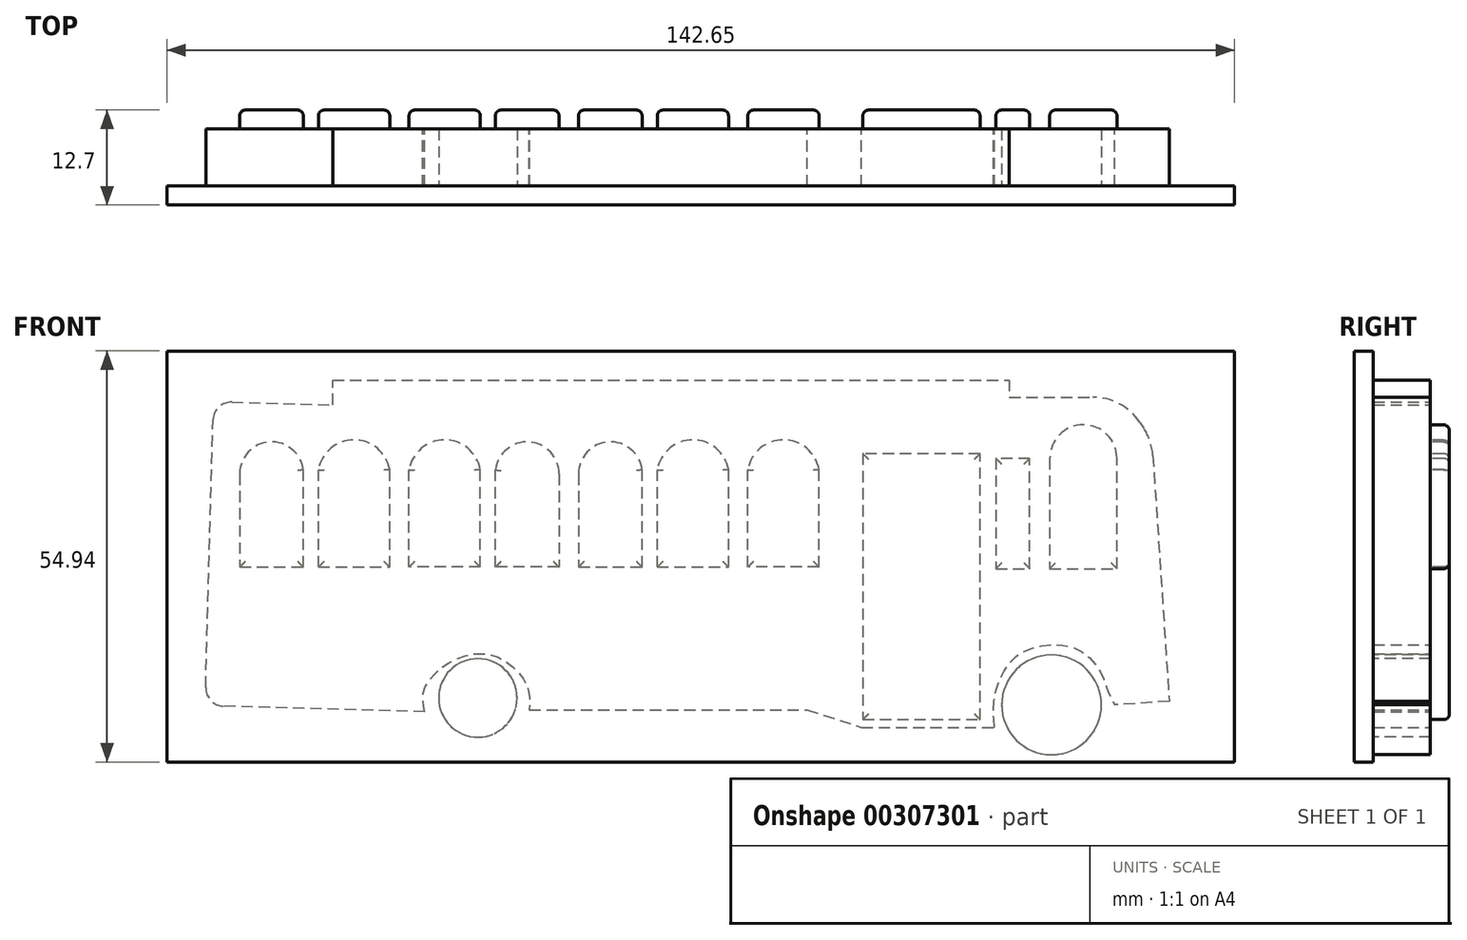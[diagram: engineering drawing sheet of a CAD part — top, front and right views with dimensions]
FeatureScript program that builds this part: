
annotation { "Feature Type Name" : "Feature", "Feature Type Description" : "" }
export const myFeature = defineFeature(function(context is Context, id is Id, definition is map)
    precondition{}
    {
        {
            var Q0;
            Q0=qCreatedBy(makeId("Front.planeOp"),FACE);
            var sketch = newSketch(context, id + "F0", { "sketchPlane" : qUnion([Q0])});
            skLineSegment(sketch, "E0", {"start": v(39.8, -36.02) * mm, "end": v(3.64, -36.02) * mm});
            skLineSegment(sketch, "E1", {"start": v(-11.3, -36.26) * mm, "end": v(-40.63, -35.46) * mm});
            skLineSegment(sketch, "E2", {"start": v(-40.63, -35.46) * mm, "end": v(-39.52, 5.2) * mm});
            skLineSegment(sketch, "E3", {"start": v(-39.52, 5.2) * mm, "end": v(-23.59, 4.75) * mm});
            skLineSegment(sketch, "E4", {"start": v(-23.59, 4.75) * mm, "end": v(-23.59, 8.08) * mm});
            skLineSegment(sketch, "E5", {"start": v(-23.59, 8.08) * mm, "end": v(66.8, 8.08) * mm});
            skLineSegment(sketch, "E6", {"start": v(66.8, 8.08) * mm, "end": v(66.8, 5.8) * mm});
            skLineSegment(sketch, "E7", {"start": v(66.8, 5.8) * mm, "end": v(81.99, 5.8) * mm});
            skLineSegment(sketch, "E8", {"start": v(81.99, 5.8) * mm, "end": v(85.84, 0) * mm});
            skLineSegment(sketch, "E9", {"start": v(85.84, 0) * mm, "end": v(88.18, -34.85) * mm});
            skLineSegment(sketch, "E10", {"start": v(88.18, -34.85) * mm, "end": v(80.86, -35.34) * mm});
            skLineSegment(sketch, "E11", {"start": v(39.8, -36.02) * mm, "end": v(47.06, -38.36) * mm});
            skLineSegment(sketch, "E12", {"start": v(47.06, -38.36) * mm, "end": v(64.81, -38.36) * mm});
            skFitSpline(sketch, "E13", {"points": [v(-11.3, -36.26) * mm, v(-11.3, -33.09) * mm, v(-6.88, -29.1) * mm, v(-1.23, -29.1) * mm, v(2.39, -32.9) * mm, v(2.67, -36.02) * mm], "startDerivative": vector(-3.97, 18.55) * mm, "endDerivative": vector(-1.35, -18.22) * mm});
            skLineSegment(sketch, "E14", {"start": v(2.67, -36.02) * mm, "end": v(3.64, -36.02) * mm});
            skFitSpline(sketch, "E15", {"points": [v(64.81, -38.36) * mm, v(64.81, -34.47) * mm, v(66.9, -29.62) * mm, v(70.47, -27.57) * mm, v(75.5, -27.75) * mm, v(78.77, -30.61) * mm, v(79.88, -33.24) * mm, v(80.86, -35.34) * mm], "startDerivative": vector(-2.47, 25.93) * mm, "endDerivative": vector(9.48, -18.57) * mm});
            skSolve(sketch);
        }
        {
            var Q0;
            Q0=makeQuery(id+"F0.imprint","IMPRINT",FACE,{"disambiguationData":[TD([[makeQuery(id+"F0.imprint","IMPRINT",EDGE,{"derivedFrom":sQuery(id+"F0.wireOp",EDGE,"E0")}),-1.0]])]});
            extrude(context, id + "F1", {"entities" : qUnion([Q0]), "depth" : 7.62 * mm});
        }
        {
            var Q0;
            Q0=makeQuery(id+"F1.opExtrude","SWEPT_EDGE",EDGE,{"disambiguationData":[OSD([sQuery(id+"F0.wireOp",EDGE,"E2"),sQuery(id+"F0.wireOp",EDGE,"E3")])]});
            var Q1;
            Q1=makeQuery(id+"F1.opExtrude","SWEPT_EDGE",EDGE,{"disambiguationData":[OSD([sQuery(id+"F0.wireOp",EDGE,"E1"),sQuery(id+"F0.wireOp",EDGE,"E2")])]});
            fillet(context, id + "F2", {"entities" : qUnion([Q0, Q1]), "radius" : 2.45 * mm, "tangentPropagation" : true, "allowEdgeOverflow" : false});
        }
        {
            var Q0;
            Q0=makeQuery(id+"F1.opExtrude","SWEPT_EDGE",EDGE,{"disambiguationData":[OSD([sQuery(id+"F0.wireOp",EDGE,"E8"),sQuery(id+"F0.wireOp",EDGE,"E9")])]});
            var Q1;
            Q1=makeQuery(id+"F1.opExtrude","SWEPT_EDGE",EDGE,{"disambiguationData":[OSD([sQuery(id+"F0.wireOp",EDGE,"E7"),sQuery(id+"F0.wireOp",EDGE,"E8")])]});
            fillet(context, id + "F3", {"entities" : qUnion([Q0, Q1]), "radius" : 7.55 * mm, "tangentPropagation" : true, "allowEdgeOverflow" : false});
        }
        {
            var Q0;
            Q0=makeQuery(id+"F1.opExtrude","CAP_FACE",FACE,{"disambiguationData":[OSD([sQuery(id+"F0.wireOp",EDGE,"E0"),sQuery(id+"F0.wireOp",EDGE,"E1"),sQuery(id+"F0.wireOp",EDGE,"E2"),sQuery(id+"F0.wireOp",EDGE,"E3"),sQuery(id+"F0.wireOp",EDGE,"E4"),sQuery(id+"F0.wireOp",EDGE,"E5"),sQuery(id+"F0.wireOp",EDGE,"E6"),sQuery(id+"F0.wireOp",EDGE,"E7"),sQuery(id+"F0.wireOp",EDGE,"E8"),sQuery(id+"F0.wireOp",EDGE,"E9"),sQuery(id+"F0.wireOp",EDGE,"E10"),sQuery(id+"F0.wireOp",EDGE,"E11"),sQuery(id+"F0.wireOp",EDGE,"E12"),sQuery(id+"F0.wireOp",EDGE,"E13"),sQuery(id+"F0.wireOp",EDGE,"E14"),sQuery(id+"F0.wireOp",EDGE,"E15")])],"isStart":false});
            var sketch = newSketch(context, id + "F4", { "sketchPlane" : qUnion([Q0])});
            skLineSegment(sketch, "E16", {"start": v(-36.02, -4.45) * mm, "end": v(-36.02, -16.93) * mm});
            skLineSegment(sketch, "E17", {"start": v(-36.02, -16.93) * mm, "end": v(-27.53, -16.93) * mm});
            skLineSegment(sketch, "E18", {"start": v(-27.53, -16.93) * mm, "end": v(-27.53, -3.96) * mm});
            skArc(sketch, "E19", {"start": v(-27.53, -3.96) * mm, "mid": v(-32, -0.2) * mm, "end": v(-36.02, -4.45) * mm});
            skLineSegment(sketch, "E20", {"start": v(47.23, -1.77) * mm, "end": v(47.23, -37.3) * mm});
            skLineSegment(sketch, "E21", {"start": v(47.23, -37.3) * mm, "end": v(62.9, -37.3) * mm});
            skLineSegment(sketch, "E22", {"start": v(62.9, -37.3) * mm, "end": v(62.9, -1.77) * mm});
            skLineSegment(sketch, "E23", {"start": v(62.9, -1.77) * mm, "end": v(47.23, -1.77) * mm});
            skLineSegment(sketch, "E24", {"start": v(47.23, -10.92) * mm, "end": v(55.06, -10.92) * mm, "construction": true});
            skLineSegment(sketch, "E25", {"start": v(55.06, -1.77) * mm, "end": v(55.06, -37.3) * mm});
            skLineSegment(sketch, "E26", {"start": v(-25.5, -16.93) * mm, "end": v(-15.98, -16.93) * mm});
            skLineSegment(sketch, "E27", {"start": v(-15.98, -16.93) * mm, "end": v(-15.98, -3.91) * mm});
            skLineSegment(sketch, "E28", {"start": v(-25.5, -16.93) * mm, "end": v(-25.5, -3.91) * mm});
            skArc(sketch, "E29", {"start": v(-15.98, -3.91) * mm, "mid": v(-20.74, 0.08) * mm, "end": v(-25.5, -3.91) * mm});
            skLineSegment(sketch, "E30", {"start": v(-14.7, 2.62) * mm, "end": v(-14.7, -16.9) * mm, "construction": true});
            skArc(sketch, "E31.MirrorCS", {"start": v(-13.4, -3.91) * mm, "mid": v(-8.64, 0.08) * mm, "end": v(-3.88, -3.91) * mm});
            skArc(sketch, "E32.MirrorCS", {"start": v(-1.86, -3.96) * mm, "mid": v(2.62, -0.2) * mm, "end": v(6.64, -4.45) * mm});
            skLineSegment(sketch, "E33.MirrorCS", {"start": v(6.64, -4.45) * mm, "end": v(6.64, -16.93) * mm});
            skLineSegment(sketch, "E34.MirrorCS", {"start": v(-1.86, -16.93) * mm, "end": v(-1.86, -3.96) * mm});
            skLineSegment(sketch, "E35.MirrorCS", {"start": v(-3.88, -16.93) * mm, "end": v(-3.88, -3.91) * mm});
            skLineSegment(sketch, "E36.MirrorCS", {"start": v(-13.4, -16.93) * mm, "end": v(-13.4, -3.91) * mm});
            skLineSegment(sketch, "E37.MirrorCS", {"start": v(-3.88, -16.93) * mm, "end": v(-13.4, -16.93) * mm});
            skLineSegment(sketch, "E38.MirrorCS", {"start": v(6.64, -16.93) * mm, "end": v(-1.86, -16.93) * mm});
            skLineSegment(sketch, "E39", {"start": v(-15.98, -9.71) * mm, "end": v(-14.7, -9.71) * mm, "construction": true});
            skLineSegment(sketch, "E40", {"start": v(6.64, -10.22) * mm, "end": v(7.94, -10.22) * mm, "construction": true});
            skLineSegment(sketch, "E41", {"start": v(7.94, -10.22) * mm, "end": v(7.94, 0) * mm, "construction": true});
            skLineSegment(sketch, "E42", {"start": v(7.94, 0) * mm, "end": v(7.94, -17.88) * mm, "construction": true});
            skArc(sketch, "E43.MirrorCS", {"start": v(17.74, -3.96) * mm, "mid": v(13.26, -0.2) * mm, "end": v(9.24, -4.45) * mm});
            skArc(sketch, "E44.MirrorCS", {"start": v(29.28, -3.91) * mm, "mid": v(24.52, 0.08) * mm, "end": v(19.76, -3.91) * mm});
            skArc(sketch, "E45.MirrorCS", {"start": v(31.87, -3.91) * mm, "mid": v(36.62, 0.08) * mm, "end": v(41.38, -3.91) * mm});
            skLineSegment(sketch, "E46.MirrorCS", {"start": v(17.74, -16.93) * mm, "end": v(17.74, -3.96) * mm});
            skLineSegment(sketch, "E47.MirrorCS", {"start": v(9.24, -4.45) * mm, "end": v(9.24, -16.93) * mm});
            skLineSegment(sketch, "E48.MirrorCS", {"start": v(19.76, -16.93) * mm, "end": v(19.76, -3.91) * mm});
            skLineSegment(sketch, "E49.MirrorCS", {"start": v(29.28, -16.93) * mm, "end": v(29.28, -3.91) * mm});
            skLineSegment(sketch, "E50.MirrorCS", {"start": v(31.87, -16.93) * mm, "end": v(31.87, -3.91) * mm});
            skLineSegment(sketch, "E51.MirrorCS", {"start": v(41.38, -16.93) * mm, "end": v(41.38, -3.91) * mm});
            skLineSegment(sketch, "E52.MirrorCS", {"start": v(41.38, -16.93) * mm, "end": v(31.87, -16.93) * mm});
            skLineSegment(sketch, "E53.MirrorCS", {"start": v(19.76, -16.93) * mm, "end": v(29.28, -16.93) * mm});
            skLineSegment(sketch, "E54.MirrorCS", {"start": v(9.24, -16.93) * mm, "end": v(17.74, -16.93) * mm});
            skLineSegment(sketch, "E55", {"start": v(65.01, -17.13) * mm, "end": v(69.53, -17.13) * mm});
            skLineSegment(sketch, "E56", {"start": v(69.53, -17.13) * mm, "end": v(69.53, -2.4) * mm});
            skLineSegment(sketch, "E57", {"start": v(69.53, -2.4) * mm, "end": v(65.01, -2.4) * mm});
            skLineSegment(sketch, "E58", {"start": v(65.01, -2.4) * mm, "end": v(65.01, -17.13) * mm});
            skLineSegment(sketch, "E59", {"start": v(71.76, -17.13) * mm, "end": v(81.84, -17.13) * mm});
            skPoint(sketch, "E59.startSnap0", {"position": v(67.27, -17.13) * mm});
            skLineSegment(sketch, "E60", {"start": v(81.84, -17.13) * mm, "end": v(81.84, -2.34) * mm});
            skLineSegment(sketch, "E61", {"start": v(71.76, -17.13) * mm, "end": v(71.76, -2.34) * mm});
            skArc(sketch, "E62", {"start": v(81.84, -2.4) * mm, "mid": v(76.88, 2.07) * mm, "end": v(71.82, -2.28) * mm});
            skSolve(sketch);
        }
        {
            var Q0;
            Q0 = qSketchRegion(id + "F4", true);
            extrude(context, id + "F5", {"entities" : qUnion([Q0]), "operationType" : NewBodyOperationType.ADD, "oppositeDirection" : true, "depth" : 10.16 * mm});
        }
        {
            var Q0;
            Q0=makeQuery(id+"F1.opExtrude","CAP_FACE",FACE,{"disambiguationData":[OSD([sQuery(id+"F0.wireOp",EDGE,"E0"),sQuery(id+"F0.wireOp",EDGE,"E1"),sQuery(id+"F0.wireOp",EDGE,"E2"),sQuery(id+"F0.wireOp",EDGE,"E3"),sQuery(id+"F0.wireOp",EDGE,"E4"),sQuery(id+"F0.wireOp",EDGE,"E5"),sQuery(id+"F0.wireOp",EDGE,"E6"),sQuery(id+"F0.wireOp",EDGE,"E7"),sQuery(id+"F0.wireOp",EDGE,"E8"),sQuery(id+"F0.wireOp",EDGE,"E9"),sQuery(id+"F0.wireOp",EDGE,"E10"),sQuery(id+"F0.wireOp",EDGE,"E11"),sQuery(id+"F0.wireOp",EDGE,"E12"),sQuery(id+"F0.wireOp",EDGE,"E13"),sQuery(id+"F0.wireOp",EDGE,"E14"),sQuery(id+"F0.wireOp",EDGE,"E15")])],"isStart":true});
            var sketch = newSketch(context, id + "F6", { "sketchPlane" : qUnion([Q0])});
            skLineSegment(sketch, "E63", {"start": v(-72.2, -17.13) * mm, "end": v(-81.18, -17.13) * mm});
            skLineSegment(sketch, "E64", {"start": v(-81.18, -17.13) * mm, "end": v(-81.18, -9.92) * mm});
            skLineSegment(sketch, "E65", {"start": v(-81.18, -9.92) * mm, "end": v(-81.18, -2.4) * mm});
            skLineSegment(sketch, "E66", {"start": v(-72.2, -2.4) * mm, "end": v(-72.2, -17.13) * mm});
            skArc(sketch, "E67", {"start": v(-72.2, -2.4) * mm, "mid": v(-76.7, 2.09) * mm, "end": v(-81.18, -2.4) * mm});
            skSolve(sketch);
        }
        {
            var Q0;
            Q0 = qSketchRegion(id + "F6", true);
            extrude(context, id + "F7", {"entities" : qUnion([Q0]), "operationType" : NewBodyOperationType.ADD, "depth" : 2.54 * mm});
        }
        {
            var Q0;
            Q0=makeQuery(id+"F1.opExtrude","CAP_FACE",FACE,{"disambiguationData":[OSD([sQuery(id+"F0.wireOp",EDGE,"E0"),sQuery(id+"F0.wireOp",EDGE,"E1"),sQuery(id+"F0.wireOp",EDGE,"E2"),sQuery(id+"F0.wireOp",EDGE,"E3"),sQuery(id+"F0.wireOp",EDGE,"E4"),sQuery(id+"F0.wireOp",EDGE,"E5"),sQuery(id+"F0.wireOp",EDGE,"E6"),sQuery(id+"F0.wireOp",EDGE,"E7"),sQuery(id+"F0.wireOp",EDGE,"E8"),sQuery(id+"F0.wireOp",EDGE,"E9"),sQuery(id+"F0.wireOp",EDGE,"E10"),sQuery(id+"F0.wireOp",EDGE,"E11"),sQuery(id+"F0.wireOp",EDGE,"E12"),sQuery(id+"F0.wireOp",EDGE,"E13"),sQuery(id+"F0.wireOp",EDGE,"E14"),sQuery(id+"F0.wireOp",EDGE,"E15")])],"isStart":false});
            var sketch = newSketch(context, id + "F8", { "sketchPlane" : qUnion([Q0])});
            skLineSegment(sketch, "E68.bottom", {"start": v(-45.74, 11.96) * mm, "end": v(96.9, 11.96) * mm});
            skLineSegment(sketch, "E68.top", {"start": v(-45.74, -42.98) * mm, "end": v(96.9, -42.98) * mm});
            skLineSegment(sketch, "E68.left", {"start": v(-45.74, 11.96) * mm, "end": v(-45.74, -42.98) * mm});
            skLineSegment(sketch, "E68.right", {"start": v(96.9, 11.96) * mm, "end": v(96.9, -42.98) * mm});
            skSolve(sketch);
        }
        {
            var Q0;
            Q0=makeQuery(id+"F8.imprint","IMPRINT",FACE,{"disambiguationData":[TD([[makeQuery(id+"F8.imprint","IMPRINT",EDGE,{"derivedFrom":sQuery(id+"F8.wireOp",EDGE,"E68.bottom")}),-1.0]])]});
            extrude(context, id + "F9", {"entities" : qUnion([Q0]), "depth" : 2.54 * mm});
        }
        {
            var Q0;
            Q0=makeQuery(id+"F1.opExtrude","CAP_FACE",FACE,{"disambiguationData":[OSD([sQuery(id+"F0.wireOp",EDGE,"E0"),sQuery(id+"F0.wireOp",EDGE,"E1"),sQuery(id+"F0.wireOp",EDGE,"E2"),sQuery(id+"F0.wireOp",EDGE,"E3"),sQuery(id+"F0.wireOp",EDGE,"E4"),sQuery(id+"F0.wireOp",EDGE,"E5"),sQuery(id+"F0.wireOp",EDGE,"E6"),sQuery(id+"F0.wireOp",EDGE,"E7"),sQuery(id+"F0.wireOp",EDGE,"E8"),sQuery(id+"F0.wireOp",EDGE,"E9"),sQuery(id+"F0.wireOp",EDGE,"E10"),sQuery(id+"F0.wireOp",EDGE,"E11"),sQuery(id+"F0.wireOp",EDGE,"E12"),sQuery(id+"F0.wireOp",EDGE,"E13"),sQuery(id+"F0.wireOp",EDGE,"E14"),sQuery(id+"F0.wireOp",EDGE,"E15")])],"isStart":false});
            extrude(context, id + "F10", {"entities" : qUnion([Q0]), "depth" : 2.54 * mm});
        }
        {
            var Q0;
            Q0=makeQuery(id+"F10.opExtrude","SWEPT_BODY",BODY,{"disambiguationData":[OSD([sQuery(id+"F0.wireOp",EDGE,"E0"),sQuery(id+"F0.wireOp",EDGE,"E1"),sQuery(id+"F0.wireOp",EDGE,"E2"),sQuery(id+"F0.wireOp",EDGE,"E3"),sQuery(id+"F0.wireOp",EDGE,"E4"),sQuery(id+"F0.wireOp",EDGE,"E5"),sQuery(id+"F0.wireOp",EDGE,"E6"),sQuery(id+"F0.wireOp",EDGE,"E7"),sQuery(id+"F0.wireOp",EDGE,"E8"),sQuery(id+"F0.wireOp",EDGE,"E9"),sQuery(id+"F0.wireOp",EDGE,"E10"),sQuery(id+"F0.wireOp",EDGE,"E11"),sQuery(id+"F0.wireOp",EDGE,"E12"),sQuery(id+"F0.wireOp",EDGE,"E13"),sQuery(id+"F0.wireOp",EDGE,"E14"),sQuery(id+"F0.wireOp",EDGE,"E15")])]});
            var Q1;
            Q1=makeQuery(id+"F9.opExtrude","SWEPT_BODY",BODY,{"disambiguationData":[OSD([sQuery(id+"F0.wireOp",EDGE,"E0"),sQuery(id+"F0.wireOp",EDGE,"E1"),sQuery(id+"F0.wireOp",EDGE,"E2"),sQuery(id+"F0.wireOp",EDGE,"E3"),sQuery(id+"F0.wireOp",EDGE,"E4"),sQuery(id+"F0.wireOp",EDGE,"E5"),sQuery(id+"F0.wireOp",EDGE,"E6"),sQuery(id+"F0.wireOp",EDGE,"E7"),sQuery(id+"F0.wireOp",EDGE,"E8"),sQuery(id+"F0.wireOp",EDGE,"E9"),sQuery(id+"F0.wireOp",EDGE,"E10"),sQuery(id+"F0.wireOp",EDGE,"E11"),sQuery(id+"F0.wireOp",EDGE,"E12"),sQuery(id+"F0.wireOp",EDGE,"E13"),sQuery(id+"F0.wireOp",EDGE,"E14"),sQuery(id+"F0.wireOp",EDGE,"E15"),sQuery(id+"F8.wireOp",EDGE,"E68.bottom"),sQuery(id+"F8.wireOp",EDGE,"E68.top"),sQuery(id+"F8.wireOp",EDGE,"E68.left"),sQuery(id+"F8.wireOp",EDGE,"E68.right")])]});
            var Q2;
            Q2=makeQuery(id+"F1.opExtrude","SWEPT_BODY",BODY,{"disambiguationData":[OSD([sQuery(id+"F0.wireOp",EDGE,"E0"),sQuery(id+"F0.wireOp",EDGE,"E1"),sQuery(id+"F0.wireOp",EDGE,"E2"),sQuery(id+"F0.wireOp",EDGE,"E3"),sQuery(id+"F0.wireOp",EDGE,"E4"),sQuery(id+"F0.wireOp",EDGE,"E5"),sQuery(id+"F0.wireOp",EDGE,"E6"),sQuery(id+"F0.wireOp",EDGE,"E7"),sQuery(id+"F0.wireOp",EDGE,"E8"),sQuery(id+"F0.wireOp",EDGE,"E9"),sQuery(id+"F0.wireOp",EDGE,"E10"),sQuery(id+"F0.wireOp",EDGE,"E11"),sQuery(id+"F0.wireOp",EDGE,"E12"),sQuery(id+"F0.wireOp",EDGE,"E13"),sQuery(id+"F0.wireOp",EDGE,"E14"),sQuery(id+"F0.wireOp",EDGE,"E15")])]});
            booleanBodies(context, id + "F11", {"operationType" : BooleanOperationType.UNION, "tools" : qUnion([Q0, Q1, Q2])});
        }
        {
            var Q0;
            Q0=makeQuery(id+"F7.opExtrude","CAP_FACE",FACE,{"disambiguationData":[OSD([sQuery(id+"F6.wireOp",EDGE,"E63"),sQuery(id+"F6.wireOp",EDGE,"E64"),sQuery(id+"F6.wireOp",EDGE,"E65"),sQuery(id+"F6.wireOp",EDGE,"E66"),sQuery(id+"F6.wireOp",EDGE,"E67")])],"isStart":false});
            var Q1;
            Q1=makeQuery(id+"F5.opExtrude","CAP_FACE",FACE,{"disambiguationData":[OSD([sQuery(id+"F4.wireOp",EDGE,"E55"),sQuery(id+"F4.wireOp",EDGE,"E56"),sQuery(id+"F4.wireOp",EDGE,"E57"),sQuery(id+"F4.wireOp",EDGE,"E58")])],"isStart":false});
            var Q2;
            Q2=makeQuery(id+"F5.opExtrude","CAP_FACE",FACE,{"disambiguationData":[OSD([sQuery(id+"F4.wireOp",EDGE,"E20"),sQuery(id+"F4.wireOp",EDGE,"E21"),sQuery(id+"F4.wireOp",EDGE,"E22"),sQuery(id+"F4.wireOp",EDGE,"E23")])],"isStart":false});
            var Q3;
            Q3=makeQuery(id+"F5.opExtrude","CAP_FACE",FACE,{"disambiguationData":[OSD([sQuery(id+"F4.wireOp",EDGE,"E45.MirrorCS"),sQuery(id+"F4.wireOp",EDGE,"E50.MirrorCS"),sQuery(id+"F4.wireOp",EDGE,"E51.MirrorCS"),sQuery(id+"F4.wireOp",EDGE,"E52.MirrorCS")])],"isStart":false});
            var Q4;
            Q4=makeQuery(id+"F5.opExtrude","CAP_FACE",FACE,{"disambiguationData":[OSD([sQuery(id+"F4.wireOp",EDGE,"E44.MirrorCS"),sQuery(id+"F4.wireOp",EDGE,"E48.MirrorCS"),sQuery(id+"F4.wireOp",EDGE,"E49.MirrorCS"),sQuery(id+"F4.wireOp",EDGE,"E53.MirrorCS")])],"isStart":false});
            var Q5;
            Q5=makeQuery(id+"F5.opExtrude","CAP_FACE",FACE,{"disambiguationData":[OSD([sQuery(id+"F4.wireOp",EDGE,"E43.MirrorCS"),sQuery(id+"F4.wireOp",EDGE,"E46.MirrorCS"),sQuery(id+"F4.wireOp",EDGE,"E47.MirrorCS"),sQuery(id+"F4.wireOp",EDGE,"E54.MirrorCS")])],"isStart":false});
            var Q6;
            Q6=makeQuery(id+"F5.opExtrude","CAP_FACE",FACE,{"disambiguationData":[OSD([sQuery(id+"F4.wireOp",EDGE,"E32.MirrorCS"),sQuery(id+"F4.wireOp",EDGE,"E33.MirrorCS"),sQuery(id+"F4.wireOp",EDGE,"E34.MirrorCS"),sQuery(id+"F4.wireOp",EDGE,"E38.MirrorCS")])],"isStart":false});
            var Q7;
            Q7=makeQuery(id+"F5.opExtrude","CAP_FACE",FACE,{"disambiguationData":[OSD([sQuery(id+"F4.wireOp",EDGE,"E31.MirrorCS"),sQuery(id+"F4.wireOp",EDGE,"E35.MirrorCS"),sQuery(id+"F4.wireOp",EDGE,"E36.MirrorCS"),sQuery(id+"F4.wireOp",EDGE,"E37.MirrorCS")])],"isStart":false});
            var Q8;
            Q8=makeQuery(id+"F5.opExtrude","CAP_FACE",FACE,{"disambiguationData":[OSD([sQuery(id+"F4.wireOp",EDGE,"E26"),sQuery(id+"F4.wireOp",EDGE,"E27"),sQuery(id+"F4.wireOp",EDGE,"E28"),sQuery(id+"F4.wireOp",EDGE,"E29")])],"isStart":false});
            var Q9;
            Q9=makeQuery(id+"F5.opExtrude","CAP_FACE",FACE,{"disambiguationData":[OSD([sQuery(id+"F4.wireOp",EDGE,"E16"),sQuery(id+"F4.wireOp",EDGE,"E17"),sQuery(id+"F4.wireOp",EDGE,"E18"),sQuery(id+"F4.wireOp",EDGE,"E19")])],"isStart":false});
            fillet(context, id + "F12", {"entities" : qUnion([Q0, Q1, Q2, Q3, Q4, Q5, Q6, Q7, Q8, Q9]), "radius" : 0.76 * mm, "tangentPropagation" : true, "allowEdgeOverflow" : false});
        }
        {
            var Q0;
            {var subQ0=sQuery(id+"F0.wireOp",EDGE,"E15");var subQ1=sQuery(id+"F0.wireOp",EDGE,"E14");var subQ2=sQuery(id+"F0.wireOp",EDGE,"E13");var subQ3=sQuery(id+"F0.wireOp",EDGE,"E12");var subQ4=sQuery(id+"F0.wireOp",EDGE,"E11");var subQ5=sQuery(id+"F0.wireOp",EDGE,"E10");var subQ6=sQuery(id+"F0.wireOp",EDGE,"E9");var subQ7=sQuery(id+"F0.wireOp",EDGE,"E8");var subQ8=sQuery(id+"F0.wireOp",EDGE,"E7");var subQ9=sQuery(id+"F0.wireOp",EDGE,"E6");var subQ10=sQuery(id+"F0.wireOp",EDGE,"E5");var subQ11=sQuery(id+"F0.wireOp",EDGE,"E4");var subQ12=sQuery(id+"F0.wireOp",EDGE,"E3");var subQ13=sQuery(id+"F0.wireOp",EDGE,"E2");var subQ14=sQuery(id+"F0.wireOp",EDGE,"E1");var subQ15=sQuery(id+"F0.wireOp",EDGE,"E0");Q0=makeQuery(id+"F11.opBoolean","MERGE",FACE,{"derivedFrom":[makeQuery(id+"F9.opExtrude","CAP_FACE",FACE,{"disambiguationData":[OSD([subQ15,subQ14,subQ13,subQ12,subQ11,subQ10,subQ9,subQ8,subQ7,subQ6,subQ5,subQ4,subQ3,subQ2,subQ1,subQ0,sQuery(id+"F8.wireOp",EDGE,"E68.bottom"),sQuery(id+"F8.wireOp",EDGE,"E68.top"),sQuery(id+"F8.wireOp",EDGE,"E68.left"),sQuery(id+"F8.wireOp",EDGE,"E68.right")])],"isStart":true}),makeQuery(id+"F10.opExtrude","CAP_FACE",FACE,{"disambiguationData":[OSD([subQ15,subQ14,subQ13,subQ12,subQ11,subQ10,subQ9,subQ8,subQ7,subQ6,subQ5,subQ4,subQ3,subQ2,subQ1,subQ0])],"isStart":true})]});}
            var sketch = newSketch(context, id + "F13", { "sketchPlane" : qUnion([Q0])});
            skCircle(sketch, "E69", {"center": v(4.2, -34.42) * mm, "radius": 5.24 * mm});
            skCircle(sketch, "E70", {"center": v(-72.45, -35.34) * mm, "radius": 6.66 * mm});
            skSolve(sketch);
        }
        {
            var Q0;
            Q0=makeQuery(id+"F13.imprint","IMPRINT",FACE,{"disambiguationData":[TD([[makeQuery(id+"F13.imprint","IMPRINT",EDGE,{"derivedFrom":sQuery(id+"F13.wireOp",EDGE,"E70")}),1.0]])]});
            var Q1;
            Q1=makeQuery(id+"F13.imprint","IMPRINT",FACE,{"disambiguationData":[TD([[makeQuery(id+"F13.imprint","IMPRINT",EDGE,{"derivedFrom":sQuery(id+"F13.wireOp",EDGE,"E69")}),1.0]])]});
            extrude(context, id + "F14", {"entities" : qUnion([Q0, Q1]), "operationType" : NewBodyOperationType.ADD, "depth" : 7.62 * mm});
        }
    });
